# Revit family: QF_DIETATEC_58011
name_source: partatom
category: Specialty Equipment
revit_build: Autodesk Revit 2016 (Build: 20150220_1215(x64)
units: mm (PartAtom-declared; Revit-internal decimal feet)

## family parameters
Always vertical = Yes
Cut with Voids When Loaded = No
OmniClass Number = 23.40.40.14
OmniClass Title = Food Service Equipment
Part Type = Normal
Room Calculation Point = No
Round Connector Dimension = Use Diameter
Shared = No
Work Plane-Based = No

## types (2) — shared parameters
Accessory = No
Assembly Code = E1090320
Cold Water Flow = 0.0 L/s
Cold Water Size = 13 mm
Cold Water Temperature Recommended = 0 °C
Conn Conduit = No
Cycle = 50 Hz
Depth Actual = 1174 mm  [stored 3.85171 ft]
Description = GENIER ACE MIXER KETTLE, 60L
Height Actual = 1080 mm  [stored 3.54331 ft]
Length Actual = 1170 mm  [stored 3.83858 ft]
Manufacturer = DIETATEC
Max Overcurrent Protection = 0 A
Min Ckt Ampacity = 0 A
Model = GENIER ACE 60 FS
URL = www.dietatec.com
Weight = 260.00 kg
zero-valued in all types: Cost

## per-type parameters (varying)
| type | Apparent Power | Electric power | FL Amps | Number of Poles | Phase | Volts |
| 58011_400V/3Ph/50Hz | 18500 VA | 18500 W | 27 A | 3 | 3 | 400 V |
| 58011_230V/1Ph/50Hz | 1000 VA | 1000 W | 4 A | 2 | 1 | 230 V |

note: [stored X ft] marks values corroborated as IEEE doubles in the binary element streams (Revit-internal decimal feet)

## geometry (parser evidence)
native form markers: Sweep x3
no freeform markers — native parametric forms only
